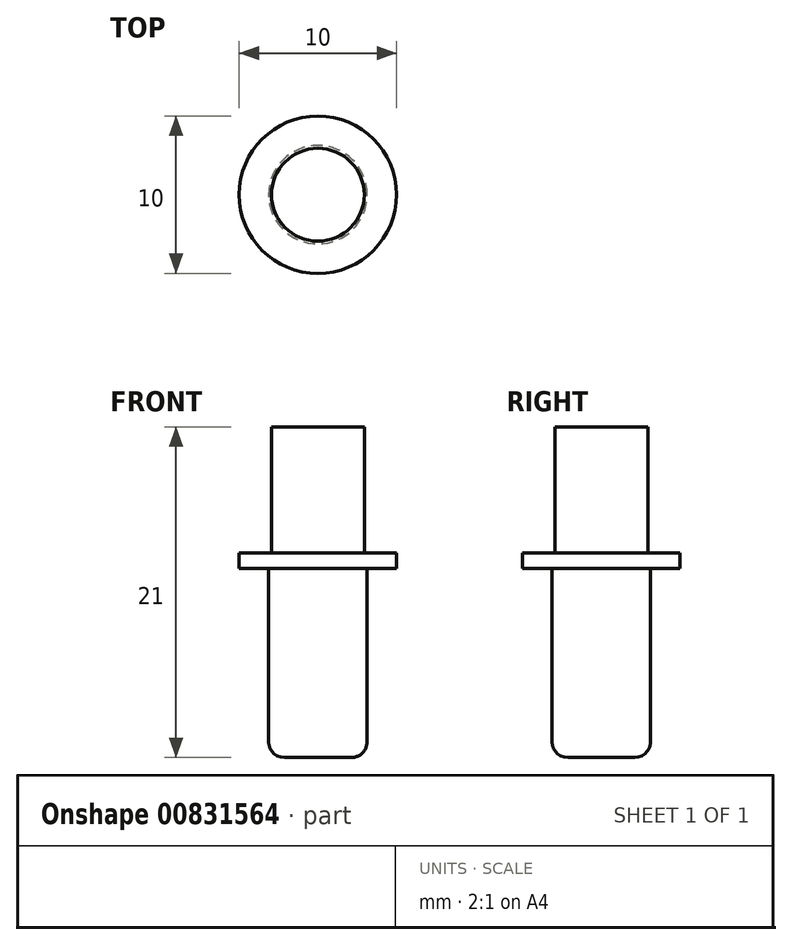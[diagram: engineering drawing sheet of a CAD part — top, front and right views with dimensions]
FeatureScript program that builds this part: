
annotation { "Feature Type Name" : "Feature", "Feature Type Description" : "" }
export const myFeature = defineFeature(function(context is Context, id is Id, definition is map)
    precondition{}
    {
        {
            var Q0;
            Q0=qCreatedBy(makeId("Top.planeOp"),FACE);
            var sketch = newSketch(context, id + "F0", { "sketchPlane" : qUnion([Q0])});
            skCircle(sketch, "E0", {"center": v(0, 0) * mm, "radius": 2.95 * mm});
            skCircle(sketch, "E1", {"center": v(0, 0) * mm, "radius": 5 * mm});
            skCircle(sketch, "E2", {"center": v(0, 0) * mm, "radius": 3.12 * mm});
            skSolve(sketch);
        }
        {
            var Q0;
            Q0=makeQuery(id+"F0.imprint","IMPRINT",FACE,{"disambiguationData":[TD([[makeQuery(id+"F0.imprint","IMPRINT",EDGE,{"derivedFrom":sQuery(id+"F0.wireOp",EDGE,"E0")}),1.0]])]});
            extrude(context, id + "F1", {"entities" : qUnion([Q0]), "depth" : 9 * mm, "offsetDistance" : 25 * mm});
        }
        {
            var Q0;
            Q0=makeQuery(id+"F0.imprint","IMPRINT",FACE,{"disambiguationData":[TD([[makeQuery(id+"F0.imprint","IMPRINT",EDGE,{"derivedFrom":sQuery(id+"F0.wireOp",EDGE,"E1")}),1.0]])]});
            var Q1;
            Q1=makeQuery(id+"F0.imprint","IMPRINT",FACE,{"disambiguationData":[TD([[makeQuery(id+"F0.imprint","IMPRINT",EDGE,{"derivedFrom":sQuery(id+"F0.wireOp",EDGE,"E0")}),-1.0]])]});
            extrude(context, id + "F2", {"entities" : qUnion([Q0, Q1]), "operationType" : NewBodyOperationType.ADD, "depth" : 1 * mm, "offsetDistance" : 25 * mm});
        }
        {
            var Q0;
            Q0=makeQuery(id+"F0.imprint","IMPRINT",FACE,{"disambiguationData":[TD([[makeQuery(id+"F0.imprint","IMPRINT",EDGE,{"derivedFrom":sQuery(id+"F0.wireOp",EDGE,"E0")}),-1.0]])]});
            var Q1;
            Q1=makeQuery(id+"F0.imprint","IMPRINT",FACE,{"disambiguationData":[TD([[makeQuery(id+"F0.imprint","IMPRINT",EDGE,{"derivedFrom":sQuery(id+"F0.wireOp",EDGE,"E0")}),1.0]])]});
            extrude(context, id + "F3", {"entities" : qUnion([Q0, Q1]), "operationType" : NewBodyOperationType.ADD, "oppositeDirection" : true, "depth" : 12 * mm, "offsetDistance" : 25 * mm});
        }
        {
            var Q0;
            Q0=makeQuery(id+"F3.opExtrude","CAP_FACE",FACE,{"disambiguationData":[OSD([sQuery(id+"F0.wireOp",EDGE,"E2")])],"isStart":false});
            fillet(context, id + "F4", {"entities" : qUnion([Q0]), "radius" : 1 * mm, "tangentPropagation" : true, "allowEdgeOverflow" : false});
        }
    });
